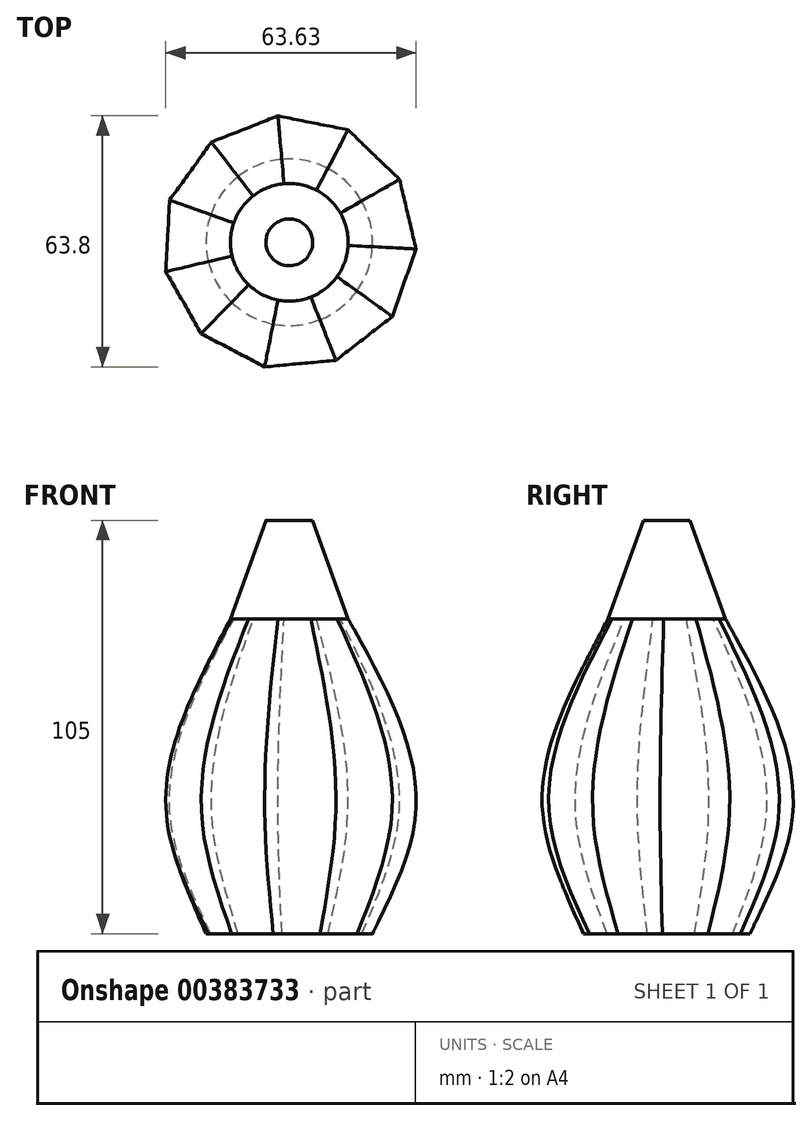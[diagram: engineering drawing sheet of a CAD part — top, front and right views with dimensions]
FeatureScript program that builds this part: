
annotation { "Feature Type Name" : "Feature", "Feature Type Description" : "" }
export const myFeature = defineFeature(function(context is Context, id is Id, definition is map)
    precondition{}
    {
        {
            var Q0;
            Q0=qCreatedBy(makeId("Top.planeOp"),FACE);
            var sketch = newSketch(context, id + "F0", { "sketchPlane" : qUnion([Q0])});
            skCircle(sketch, "E0", {"center": v(0, 0) * mm, "radius": 21.15 * mm});
            skSolve(sketch);
        }
        {
            var Q0;
            Q0=qCreatedBy(makeId("Top.planeOp"),FACE);
            cPlane(context, id + "F1", {"entities" : qUnion([Q0]), "cplaneType" : CPlaneType.OFFSET, "offset" : 30 * mm, "width" : 152.4 * mm, "height" : 152.4 * mm});
        }
        {
            var Q0;
            Q0=qCreatedBy(id+"F1.planeOp",FACE);
            var sketch = newSketch(context, id + "F2", { "sketchPlane" : qUnion([Q0])});
            skCircle(sketch, "E1.cCircle", {"center": v(0, 0) * mm, "radius": 32.09 * mm, "construction": true});
            skLineSegment(sketch, "E1.0", {"start": v(27.87, 15.9) * mm, "end": v(32.04, -1.69) * mm});
            skLineSegment(sketch, "E1.1", {"start": v(32.04, -1.69) * mm, "end": v(26.04, -18.74) * mm});
            skLineSegment(sketch, "E1.2", {"start": v(26.04, -18.74) * mm, "end": v(11.77, -29.85) * mm});
            skLineSegment(sketch, "E1.3", {"start": v(11.77, -29.85) * mm, "end": v(-6.23, -31.48) * mm});
            skLineSegment(sketch, "E1.4", {"start": v(-6.23, -31.48) * mm, "end": v(-22.26, -23.1) * mm});
            skLineSegment(sketch, "E1.5", {"start": v(-22.26, -23.1) * mm, "end": v(-31.22, -7.4) * mm});
            skLineSegment(sketch, "E1.6", {"start": v(-31.22, -7.4) * mm, "end": v(-30.27, 10.65) * mm});
            skLineSegment(sketch, "E1.7", {"start": v(-30.27, 10.65) * mm, "end": v(-19.7, 25.32) * mm});
            skLineSegment(sketch, "E1.8", {"start": v(-19.7, 25.32) * mm, "end": v(-2.89, 31.96) * mm});
            skLineSegment(sketch, "E1.9", {"start": v(-2.89, 31.96) * mm, "end": v(14.85, 28.44) * mm});
            skLineSegment(sketch, "E1.10", {"start": v(14.85, 28.44) * mm, "end": v(27.87, 15.9) * mm});
            skSolve(sketch);
        }
        {
            var Q0;
            Q0=qCreatedBy(id+"F1.planeOp",FACE);
            cPlane(context, id + "F3", {"entities" : qUnion([Q0]), "cplaneType" : CPlaneType.OFFSET, "offset" : 50 * mm, "width" : 150 * mm, "height" : 150 * mm});
        }
        {
            var Q0;
            Q0=qCreatedBy(id+"F3.planeOp",FACE);
            var sketch = newSketch(context, id + "F4", { "sketchPlane" : qUnion([Q0])});
            skPoint(sketch, "E2.middle", {"position": v(0, 0) * mm});
            skCircle(sketch, "E3", {"center": v(0, 0) * mm, "radius": 14.94 * mm});
            skSolve(sketch);
        }
        {
            var Q0;
            Q0=makeQuery(id+"F0.imprint","IMPRINT",FACE,{"disambiguationData":[TD([[makeQuery(id+"F0.imprint","IMPRINT",EDGE,{"derivedFrom":sQuery(id+"F0.wireOp",EDGE,"E0")}),1.0]])]});
            var Q1;
            Q1=makeQuery(id+"F2.imprint","IMPRINT",FACE,{"disambiguationData":[TD([[makeQuery(id+"F2.imprint","IMPRINT",EDGE,{"derivedFrom":sQuery(id+"F2.wireOp",EDGE,"E1.0")}),-1.0]])]});
            var Q2;
            Q2=makeQuery(id+"F4.imprint","IMPRINT",FACE,{"disambiguationData":[TD([[makeQuery(id+"F4.imprint","IMPRINT",EDGE,{"derivedFrom":sQuery(id+"F4.wireOp",EDGE,"E3")}),1.0]])]});
            loft(context, id + "F5", {"sheetProfilesArray" : [{ "sheetProfileEntities" : qUnion([Q0]) }, { "sheetProfileEntities" : qUnion([Q1]) }, { "sheetProfileEntities" : qUnion([Q2]) }]});
        }
        {
            var Q0;
            Q0=qCreatedBy(id+"F3.planeOp",FACE);
            var Q1;
            Q1 = qBodyType(qCreatedBy(id + "Fm4J6iV5THcnpvU_1" ,EDGE), BodyType.WIRE);
            cPlane(context, id + "F6", {"entities" : qUnion([Q0, Q1]), "cplaneType" : CPlaneType.OFFSET, "offset" : 25 * mm, "width" : 150 * mm, "height" : 150 * mm});
        }
        {
            var Q0;
            Q0=qCreatedBy(id+"F6.planeOp",FACE);
            var sketch = newSketch(context, id + "F7", { "sketchPlane" : qUnion([Q0])});
            skCircle(sketch, "E4", {"center": v(0, 0) * mm, "radius": 5.94 * mm});
            skSolve(sketch);
        }
        {
            var Q1;
            Q1=makeQuery(id+"F5.opLoft","CAP_FACE",FACE,{"disambiguationData":[OSD([makeQuery(id+"F4.imprint","IMPRINT",FACE,{"disambiguationData":[TD([[makeQuery(id+"F4.imprint","IMPRINT",EDGE,{"derivedFrom":sQuery(id+"F4.wireOp",EDGE,"E3")}),1.0]])]})])],"isStart":true});
            var Q2;
            Q2=makeQuery(id+"F7.imprint","IMPRINT",FACE,{"disambiguationData":[TD([[makeQuery(id+"F7.imprint","IMPRINT",EDGE,{"derivedFrom":sQuery(id+"F7.wireOp",EDGE,"E4")}),1.0]])]});
            loft(context, id + "F8", {"operationType" : NewBodyOperationType.ADD, "sheetProfilesArray" : [{ "sheetProfileEntities" : qUnion([Q1]) }, { "sheetProfileEntities" : qUnion([Q2]) }]});
        }
    });
